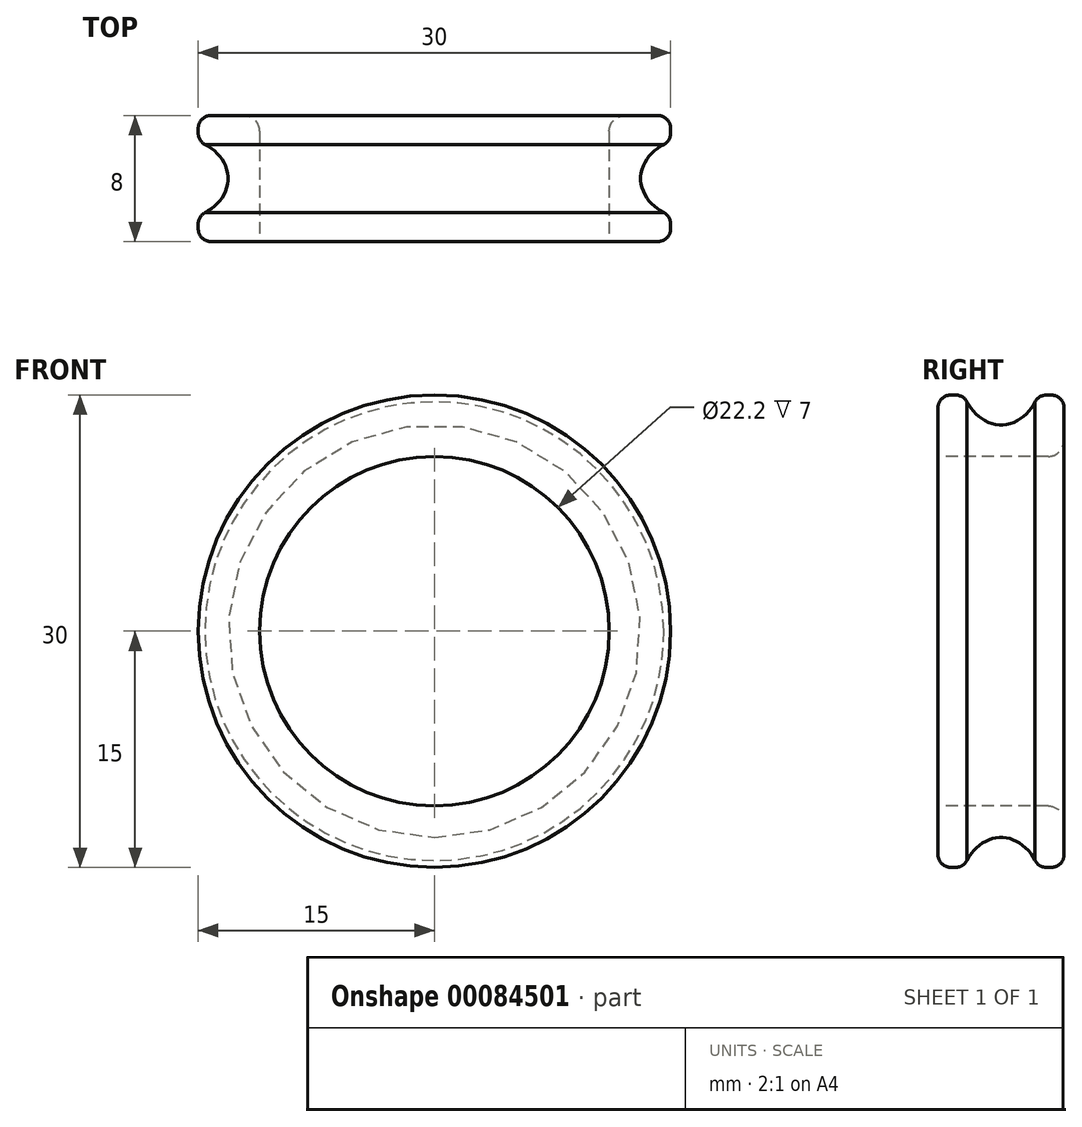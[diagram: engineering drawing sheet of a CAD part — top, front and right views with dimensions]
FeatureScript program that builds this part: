
annotation { "Feature Type Name" : "Feature", "Feature Type Description" : "" }
export const myFeature = defineFeature(function(context is Context, id is Id, definition is map)
    precondition{}
    {
        {
            var Q0;
            Q0=qCreatedBy(makeId("Right.planeOp"),FACE);
            var sketch = newSketch(context, id + "F0", { "sketchPlane" : qUnion([Q0])});
            skLineSegment(sketch, "E0.bottom", {"start": v(4, -1) * mm, "end": v(-4, -1) * mm});
            skLineSegment(sketch, "E0.top", {"start": v(4, 1) * mm, "end": v(-4, 1) * mm});
            skLineSegment(sketch, "E0.left", {"start": v(4, -1) * mm, "end": v(4, 1) * mm});
            skLineSegment(sketch, "E0.right", {"start": v(-4, -1) * mm, "end": v(-4, 1) * mm});
            skPoint(sketch, "E0.middle", {"position": v(0, 0) * mm});
            skLineSegment(sketch, "E1", {"start": v(0, 1) * mm, "end": v(0, 4.3) * mm});
            skLineSegment(sketch, "E2", {"start": v(4, 1) * mm, "end": v(4, 4.3) * mm});
            skLineSegment(sketch, "E3", {"start": v(-4, 1) * mm, "end": v(-4, 4.3) * mm});
            skLineSegment(sketch, "E4.left", {"start": v(-4, 1) * mm, "end": v(-4, -1) * mm});
            skLineSegment(sketch, "E5.left", {"start": v(-4, -1) * mm, "end": v(-4, -4.4) * mm});
            skLineSegment(sketch, "E6", {"start": v(0, 4.3) * mm, "end": v(2.6, 4.3) * mm});
            skEllipse(sketch, "E7", {"center": v(0, 4.3) * mm, "majorRadius": 3.3 * mm, "minorRadius": 2.6 * mm, "majorAxis": v(0, -1)});
            skLineSegment(sketch, "E8", {"start": v(4, 4.3) * mm, "end": v(-4, 4.3) * mm});
            skLineSegment(sketch, "E9.bottom", {"start": v(-4, -4.4) * mm, "end": v(4, -4.4) * mm});
            skLineSegment(sketch, "E9.top", {"start": v(-4, -12.1) * mm, "end": v(4, -12.1) * mm});
            skLineSegment(sketch, "E9.left", {"start": v(-4, -4.4) * mm, "end": v(-4, -12.1) * mm});
            skLineSegment(sketch, "E9.right", {"start": v(4, -4.4) * mm, "end": v(4, -12.1) * mm});
            skLineSegment(sketch, "E10.bottom", {"start": v(-4, -1) * mm, "end": v(-3.1, -1) * mm});
            skLineSegment(sketch, "E10.top", {"start": v(-4, -4.4) * mm, "end": v(-3.1, -4.4) * mm});
            skLineSegment(sketch, "E10.right", {"start": v(-3.1, -1) * mm, "end": v(-3.1, -4.4) * mm});
            skPoint(sketch, "E11", {"position": v(-2.6, 4.3) * mm});
            skLineSegment(sketch, "E12", {"start": v(4, 2.9) * mm, "end": v(-4, 2.9) * mm});
            skPoint(sketch, "E13", {"position": v(-2.35, 2.9) * mm});
            skPoint(sketch, "E14", {"position": v(2.35, 2.9) * mm});
            skSolve(sketch);
        }
        {
            var Q0;
            {var subQ1=sQuery(id+"F0.wireOp",EDGE,"E2");var subQ3=sQuery(id+"F0.wireOp",EDGE,"E12");var subQ4=makeQuery(id+"F0.imprint","INTERSECT",VERTEX,{"derivedFrom":[subQ1,subQ3]});Q0=makeQuery(id+"F0.imprint","IMPRINT",FACE,{"disambiguationData":[TD([[makeQuery(id+"F0.imprint","IMPRINT",EDGE,{"disambiguationData":[TD([[subQ4,-1.0]])],"derivedFrom":subQ3}),1.0]])]});}
            var Q1;
            Q1=makeQuery(id+"F0.imprint","IMPRINT",FACE,{"disambiguationData":[TD([[makeQuery(id+"F0.imprint","IMPRINT",EDGE,{"derivedFrom":sQuery(id+"F0.wireOp",EDGE,"E0.bottom")}),-1.0]])]});
            var Q2;
            {var subQ1=sQuery(id+"F0.wireOp",EDGE,"E3");var subQ3=sQuery(id+"F0.wireOp",EDGE,"E12");var subQ4=makeQuery(id+"F0.imprint","INTERSECT",VERTEX,{"derivedFrom":[subQ1,subQ3]});Q2=makeQuery(id+"F0.imprint","IMPRINT",FACE,{"disambiguationData":[TD([[makeQuery(id+"F0.imprint","IMPRINT",EDGE,{"disambiguationData":[TD([[subQ4,1.0]])],"derivedFrom":subQ3}),1.0]])]});}
            var Q3;
            Q3=makeQuery(id+"F0.imprint","IMPRINT",FACE,{"disambiguationData":[TD([[makeQuery(id+"F0.imprint","IMPRINT",EDGE,{"derivedFrom":sQuery(id+"F0.wireOp",EDGE,"E10.bottom")}),-1.0]])]});
            var Q4;
            Q4=sQuery(id+"F0.wireOp",EDGE,"E9.top");
            revolve(context, id + "F1", {"entities" : qUnion([Q0, Q1, Q2, Q3]), "axis" : qUnion([Q4]), "revolveType" : RevolveType.FULL});
        }
        {
            var Q0;
            Q0=makeQuery(id+"F1.opRevolve","SWEPT_EDGE",EDGE,{"disambiguationData":[OSD([sQuery(id+"F0.wireOp",EDGE,"E2"),sQuery(id+"F0.wireOp",EDGE,"E12")])]});
            var Q1;
            Q1=makeQuery(id+"F1.opRevolve","SWEPT_EDGE",EDGE,{"disambiguationData":[OSD([sQuery(id+"F0.wireOp",EDGE,"E3"),sQuery(id+"F0.wireOp",EDGE,"E12")])]});
            var Q2;
            Q2=makeQuery(id+"F1.opRevolve","SWEPT_EDGE",EDGE,{"disambiguationData":[OSD([sQuery(id+"F0.wireOp",EDGE,"E3"),sQuery(id+"F0.wireOp",EDGE,"E12")])]});
            var Q3;
            {var subQ0=sQuery(id+"F0.wireOp",EDGE,"E12");var subQ1=sQuery(id+"F0.wireOp",EDGE,"E7");Q3=makeQuery(id+"F1.opRevolve","SWEPT_EDGE",EDGE,{"disambiguationData":[OSD([subQ1,subQ0]),TDD([makeQuery(id+"F0.imprint","INTERSECT",VERTEX,{"disambiguationData":[OD(0.0)],"derivedFrom":[subQ1,subQ0]})])]});}
            var Q4;
            {var subQ0=sQuery(id+"F0.wireOp",EDGE,"E12");var subQ1=sQuery(id+"F0.wireOp",EDGE,"E7");Q4=makeQuery(id+"F1.opRevolve","SWEPT_EDGE",EDGE,{"disambiguationData":[OSD([subQ1,subQ0]),TDD([makeQuery(id+"F0.imprint","INTERSECT",VERTEX,{"disambiguationData":[OD(1.0)],"derivedFrom":[subQ1,subQ0]})])]});}
            fillet(context, id + "F2", {"entities" : qUnion([Q0, Q1, Q2, Q3, Q4]), "radius" : 0.8 * mm, "tangentPropagation" : true, "allowEdgeOverflow" : false});
        }
        {
            var Q0;
            Q0=makeQuery(id+"F1.opRevolve","SWEPT_EDGE",EDGE,{"disambiguationData":[OSD([sQuery(id+"F0.wireOp",EDGE,"E0.bottom"),sQuery(id+"F0.wireOp",EDGE,"E0.left")])]});
            fillet(context, id + "F3", {"entities" : qUnion([Q0]), "radius" : 1 * mm, "tangentPropagation" : true, "allowEdgeOverflow" : false});
        }
    });
